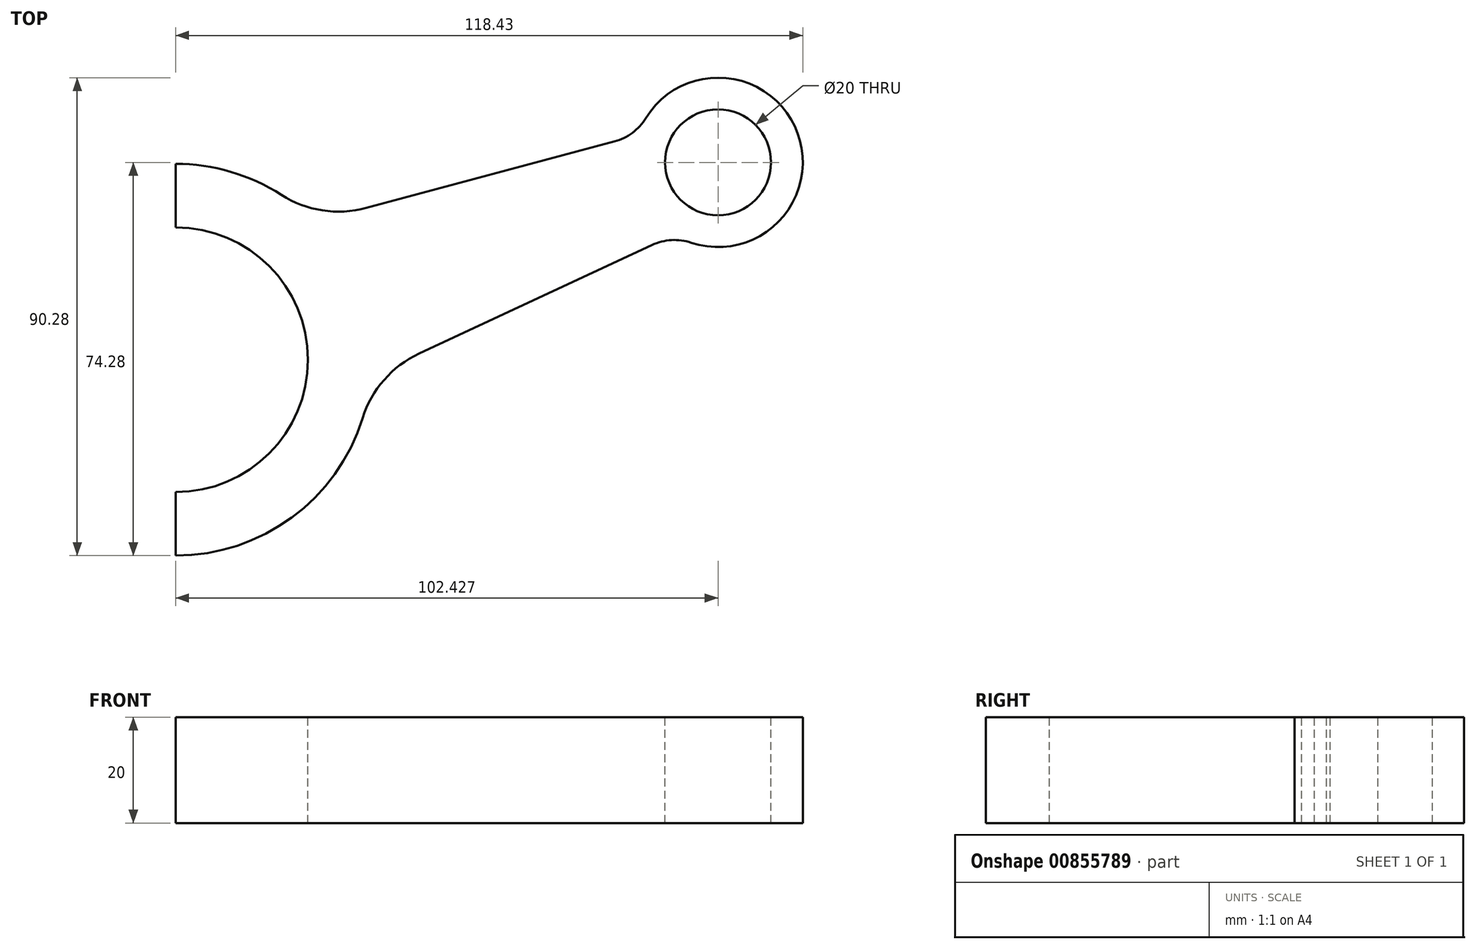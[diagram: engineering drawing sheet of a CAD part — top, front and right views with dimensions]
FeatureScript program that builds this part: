
annotation { "Feature Type Name" : "Feature", "Feature Type Description" : "" }
export const myFeature = defineFeature(function(context is Context, id is Id, definition is map)
    precondition{}
    {
        {
            var Q0;
            Q0=qCreatedBy(makeId("Top.planeOp"),FACE);
            var sketch = newSketch(context, id + "F0", { "sketchPlane" : qUnion([Q0])});
            skArc(sketch, "E0", {"start": v(0, -25) * mm, "mid": v(25, 0) * mm, "end": v(0, 25) * mm});
            skCircle(sketch, "E1", {"center": v(102.43, 37.28) * mm, "radius": 10 * mm});
            skArc(sketch, "E2", {"start": v(0, -37) * mm, "mid": v(25.05, -27.23) * mm, "end": v(36.87, -3.08) * mm});
            skArc(sketch, "E3", {"start": v(94.1, 23.61) * mm, "mid": v(117.46, 42.75) * mm, "end": v(87.27, 42.4) * mm});
            skPoint(sketch, "E4.end.orphan", {"position": v(27.66, 24.58) * mm});
            skPoint(sketch, "E4.start.orphan", {"position": v(105.77, 52.93) * mm});
            skPoint(sketch, "E5.MirrorCS.end.orphan", {"position": v(702.5, -624.27) * mm});
            skPoint(sketch, "E5.MirrorCS.start.orphan", {"position": v(3210.42, -404.85) * mm});
            skLineSegment(sketch, "E6", {"start": v(87.27, 42.4) * mm, "end": v(26.27, 26.06) * mm});
            skLineSegment(sketch, "E7.MirrorCS", {"start": v(94.1, 23.61) * mm, "end": v(36.87, -3.08) * mm});
            skLineSegment(sketch, "E8", {"start": v(0, 37) * mm, "end": v(0, 25) * mm});
            skPoint(sketch, "E9.orphan", {"position": v(0, 2266.2) * mm});
            skLineSegment(sketch, "E10.trimOffspring", {"start": v(0, -25) * mm, "end": v(0, -37) * mm});
            skArc(sketch, "E11.trimOffspring", {"start": v(26.27, 26.06) * mm, "mid": v(14.23, 34.16) * mm, "end": v(0, 37) * mm});
            skLineSegment(sketch, "E12", {"start": v(0, 0) * mm, "end": v(117.46, 42.75) * mm, "construction": true});
            skLineSegment(sketch, "E13", {"start": v(0, 0) * mm, "end": v(118.65, 0) * mm, "construction": true});
            skSolve(sketch);
        }
        {
            var Q0;
            Q0 = qSketchRegion(id + "F0", true);
            extrude(context, id + "F1", {"entities" : qUnion([Q0]), "oppositeDirection" : true, "depth" : 10 * mm, "offsetDistance" : 25.4 * mm, "hasSecondDirection" : true, "secondDirectionOppositeDirection" : false, "secondDirectionDepth" : 10 * mm});
        }
        {
            var Q0;
            Q0=makeQuery(id+"F1.opExtrude","SWEPT_EDGE",EDGE,{"disambiguationData":[OSD([sQuery(id+"F0.wireOp",EDGE,"E6"),sQuery(id+"F0.wireOp",EDGE,"E11.trimOffspring")])]});
            var Q1;
            Q1=makeQuery(id+"F1.opExtrude","SWEPT_EDGE",EDGE,{"disambiguationData":[OSD([sQuery(id+"F0.wireOp",EDGE,"E2"),sQuery(id+"F0.wireOp",EDGE,"E7.MirrorCS")])]});
            fillet(context, id + "F2", {"entities" : qUnion([Q0, Q1]), "radius" : 20 * mm, "tangentPropagation" : true, "allowEdgeOverflow" : false});
        }
        {
            var Q0;
            Q0=makeQuery(id+"F1.opExtrude","SWEPT_EDGE",EDGE,{"disambiguationData":[OSD([sQuery(id+"F0.wireOp",EDGE,"E3"),sQuery(id+"F0.wireOp",EDGE,"E6")])]});
            var Q1;
            Q1=makeQuery(id+"F1.opExtrude","SWEPT_EDGE",EDGE,{"disambiguationData":[OSD([sQuery(id+"F0.wireOp",EDGE,"E3"),sQuery(id+"F0.wireOp",EDGE,"E7.MirrorCS")])]});
            fillet(context, id + "F3", {"entities" : qUnion([Q0, Q1]), "radius" : 10 * mm, "tangentPropagation" : true, "allowEdgeOverflow" : false});
        }
    });
